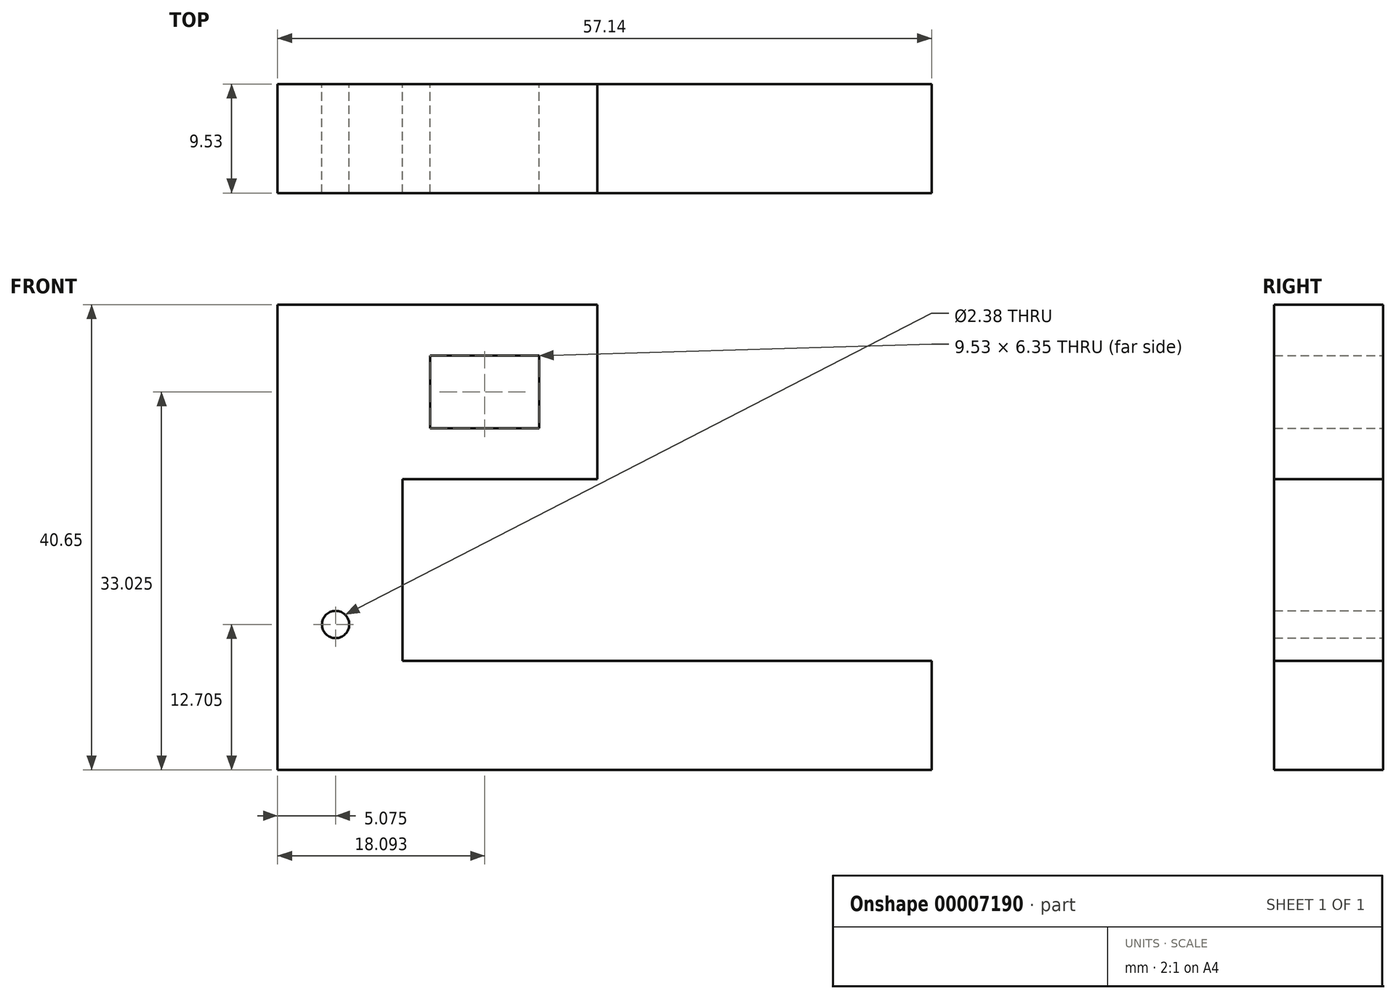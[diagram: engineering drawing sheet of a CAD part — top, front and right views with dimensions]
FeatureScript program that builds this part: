
annotation { "Feature Type Name" : "Feature", "Feature Type Description" : "" }
export const myFeature = defineFeature(function(context is Context, id is Id, definition is map)
    precondition{}
    {
        {
            var Q0;
            Q0=qCreatedBy(makeId("Front.planeOp"),FACE);
            var sketch = newSketch(context, id + "F0", { "sketchPlane" : qUnion([Q0])});
            skLineSegment(sketch, "E0", {"start": v(-13.34, 31.12) * mm, "end": v(-13.34, -9.53) * mm});
            skLineSegment(sketch, "E1", {"start": v(-13.34, -9.53) * mm, "end": v(43.81, -9.52) * mm});
            skLineSegment(sketch, "E2", {"start": v(43.81, -9.52) * mm, "end": v(43.81, 0) * mm});
            skLineSegment(sketch, "E3", {"start": v(14.6, 31.12) * mm, "end": v(-13.34, 31.12) * mm});
            skLineSegment(sketch, "E4.bottom", {"start": v(0, 26.67) * mm, "end": v(9.52, 26.67) * mm});
            skLineSegment(sketch, "E4.top", {"start": v(0, 20.32) * mm, "end": v(9.52, 20.32) * mm});
            skLineSegment(sketch, "E4.left", {"start": v(0, 26.67) * mm, "end": v(0, 20.32) * mm});
            skLineSegment(sketch, "E4.right", {"start": v(9.52, 26.67) * mm, "end": v(9.52, 20.32) * mm});
            skCircle(sketch, "E5", {"center": v(-8.26, 3.17) * mm, "radius": 1.2 * mm});
            skLineSegment(sketch, "E6", {"start": v(14.6, 31.12) * mm, "end": v(14.6, 15.88) * mm});
            skLineSegment(sketch, "E7", {"start": v(14.6, 15.88) * mm, "end": v(-2.42, 15.88) * mm});
            skLineSegment(sketch, "E8", {"start": v(-2.42, 15.88) * mm, "end": v(-2.42, 0) * mm});
            skLineSegment(sketch, "E9", {"start": v(-2.42, 0) * mm, "end": v(43.81, 0) * mm});
            skSolve(sketch);
        }
        {
            var Q0;
            Q0=makeQuery(id+"F0.imprint","IMPRINT",FACE,{"disambiguationData":[TD([[makeQuery(id+"F0.imprint","IMPRINT",EDGE,{"derivedFrom":sQuery(id+"F0.wireOp",EDGE,"E0")}),1.0]])]});
            extrude(context, id + "F1", {"entities" : qUnion([Q0]), "depth" : 9.52 * mm});
        }
    });
